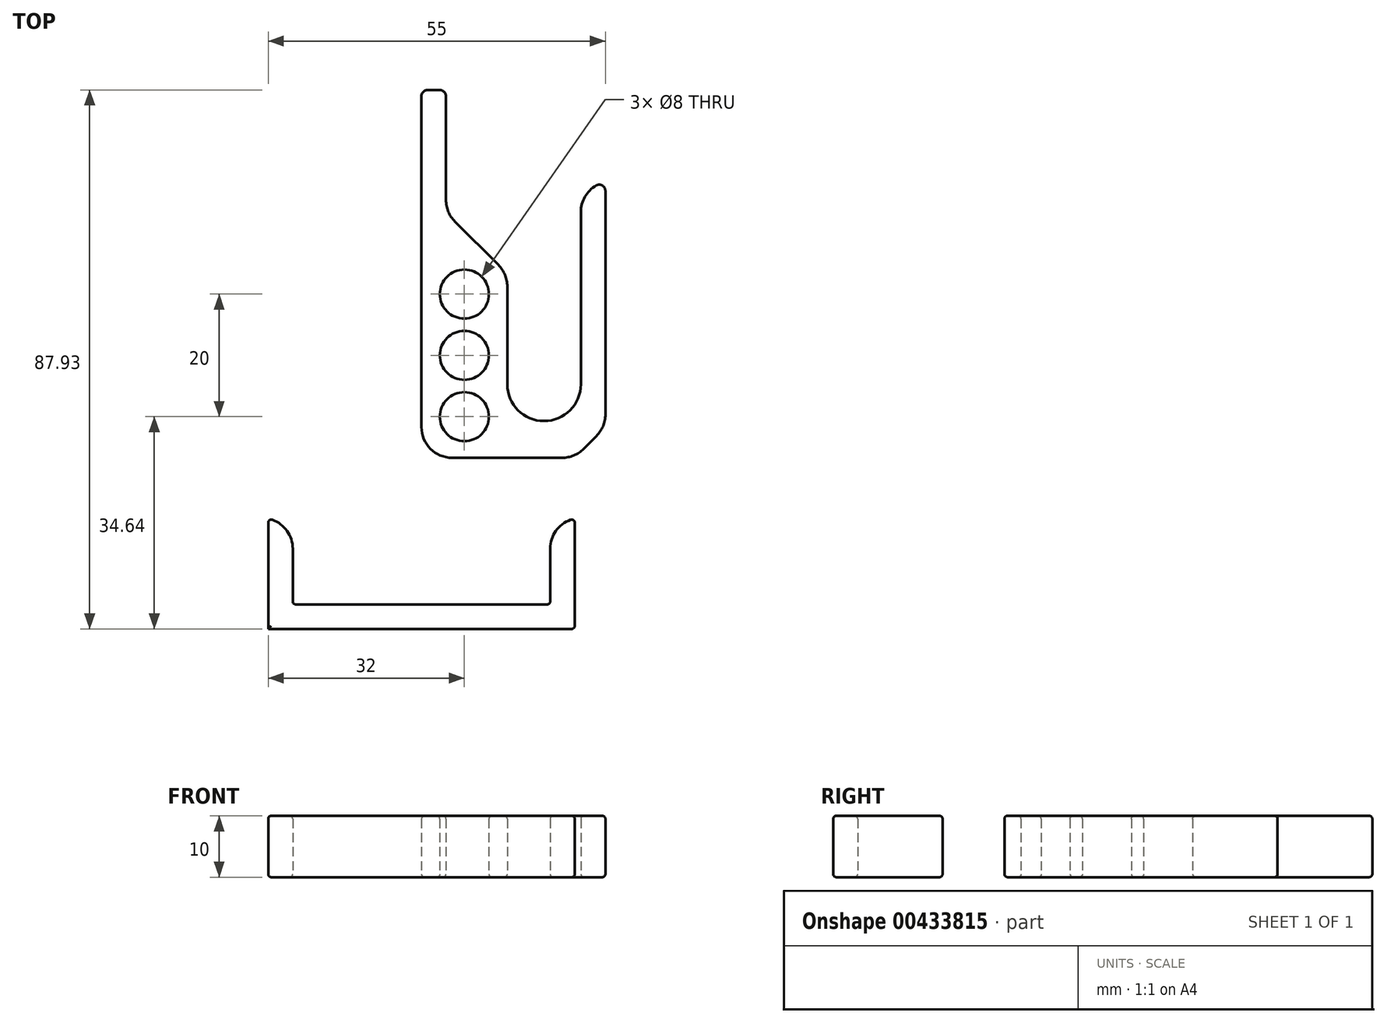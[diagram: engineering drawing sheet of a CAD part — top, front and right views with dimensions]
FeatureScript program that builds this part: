
annotation { "Feature Type Name" : "Feature", "Feature Type Description" : "" }
export const myFeature = defineFeature(function(context is Context, id is Id, definition is map)
    precondition{}
    {
        {
            var Q0;
            Q0=qCreatedBy(makeId("Top.planeOp"),FACE);
            var sketch = newSketch(context, id + "F0", { "sketchPlane" : qUnion([Q0])});
            skLineSegment(sketch, "E0", {"start": v(0, 35.79) * mm, "end": v(0, -24.21) * mm});
            skLineSegment(sketch, "E1", {"start": v(0, -24.21) * mm, "end": v(25, -24.21) * mm});
            skLineSegment(sketch, "E2", {"start": v(25, -24.21) * mm, "end": v(30, -19.21) * mm});
            skLineSegment(sketch, "E3", {"start": v(30, -19.21) * mm, "end": v(30, 20.79) * mm});
            skLineSegment(sketch, "E4", {"start": v(30, 20.79) * mm, "end": v(26, 20.79) * mm});
            skLineSegment(sketch, "E5", {"start": v(26, 20.79) * mm, "end": v(26, -12.21) * mm});
            skLineSegment(sketch, "E6", {"start": v(14, -12.21) * mm, "end": v(14, 5.79) * mm});
            skLineSegment(sketch, "E7", {"start": v(4, 35.79) * mm, "end": v(0, 35.79) * mm});
            skLineSegment(sketch, "E8", {"start": v(14, 5.79) * mm, "end": v(4, 15.79) * mm});
            skLineSegment(sketch, "E9", {"start": v(4, 15.79) * mm, "end": v(4, 35.79) * mm});
            skArc(sketch, "E10", {"start": v(14, -12.21) * mm, "mid": v(20, -18.21) * mm, "end": v(26, -12.21) * mm});
            skSolve(sketch);
        }
        {
            var Q0;
            Q0 = qSketchRegion(id + "F0", true);
            extrude(context, id + "F1", {"entities" : qUnion([Q0]), "depth" : 10 * mm});
        }
        {
            var Q0;
            Q0=makeQuery(id+"F1.opExtrude","SWEPT_EDGE",EDGE,{"disambiguationData":[OSD([sQuery(id+"F0.wireOp",EDGE,"E2"),sQuery(id+"F0.wireOp",EDGE,"E3")])]});
            var Q1;
            Q1=makeQuery(id+"F1.opExtrude","SWEPT_EDGE",EDGE,{"disambiguationData":[OSD([sQuery(id+"F0.wireOp",EDGE,"E1"),sQuery(id+"F0.wireOp",EDGE,"E2")])]});
            var Q2;
            Q2=makeQuery(id+"F1.opExtrude","SWEPT_EDGE",EDGE,{"disambiguationData":[OSD([sQuery(id+"F0.wireOp",EDGE,"E0"),sQuery(id+"F0.wireOp",EDGE,"E1")])]});
            var Q3;
            Q3=makeQuery(id+"F1.opExtrude","SWEPT_EDGE",EDGE,{"disambiguationData":[OSD([sQuery(id+"F0.wireOp",EDGE,"k2jaiBP4-kXWV-sNBi-WAxK-4QkH4Nh1HUbv"),sQuery(id+"F0.wireOp",EDGE,"E6")])]});
            var Q4;
            Q4=makeQuery(id+"F1.opExtrude","SWEPT_EDGE",EDGE,{"disambiguationData":[OSD([sQuery(id+"F0.wireOp",EDGE,"0vQgTybP-b8qj-oL10-YA1z-iEbFXQybWoTR"),sQuery(id+"F0.wireOp",EDGE,"k2jaiBP4-kXWV-sNBi-WAxK-4QkH4Nh1HUbv")])]});
            var Q5;
            Q5=makeQuery(id+"F1.opExtrude","SWEPT_EDGE",EDGE,{"disambiguationData":[OSD([sQuery(id+"F0.wireOp",EDGE,"E5"),sQuery(id+"F0.wireOp",EDGE,"0vQgTybP-b8qj-oL10-YA1z-iEbFXQybWoTR")])]});
            var Q6;
            Q6=makeQuery(id+"F1.opExtrude","SWEPT_EDGE",EDGE,{"disambiguationData":[OSD([sQuery(id+"F0.wireOp",EDGE,"E4"),sQuery(id+"F0.wireOp",EDGE,"E5")])]});
            var Q7;
            Q7=makeQuery(id+"F1.opExtrude","SWEPT_EDGE",EDGE,{"disambiguationData":[OSD([sQuery(id+"F0.wireOp",EDGE,"E6"),sQuery(id+"F0.wireOp",EDGE,"E8")])]});
            var Q8;
            Q8=makeQuery(id+"F1.opExtrude","SWEPT_EDGE",EDGE,{"disambiguationData":[OSD([sQuery(id+"F0.wireOp",EDGE,"E8"),sQuery(id+"F0.wireOp",EDGE,"E9")])]});
            fillet(context, id + "F2", {"entities" : qUnion([Q0, Q1, Q2, Q3, Q4, Q5, Q6, Q7, Q8]), "radius" : 5 * mm, "tangentPropagation" : true, "allowEdgeOverflow" : false});
        }
        {
            var Q0;
            Q0=makeQuery(id+"F2.opFillet","BLEND_EDGE",EDGE,{"blendedFrom":[makeQuery(id+"F1.opExtrude","SWEPT_EDGE",EDGE,{"disambiguationData":[OSD([sQuery(id+"F0.wireOp",EDGE,"E4"),sQuery(id+"F0.wireOp",EDGE,"E5")])]}),makeQuery(id+"F1.opExtrude","SWEPT_FACE",FACE,{"disambiguationData":[OSD([sQuery(id+"F0.wireOp",EDGE,"E3")])]})],"blendedInto":[makeQuery(id+"F1.opExtrude","SWEPT_FACE",FACE,{"disambiguationData":[OSD([sQuery(id+"F0.wireOp",EDGE,"E3")])]})]});
            var Q1;
            Q1=makeQuery(id+"F1.opExtrude","SWEPT_EDGE",EDGE,{"disambiguationData":[OSD([sQuery(id+"F0.wireOp",EDGE,"E0"),sQuery(id+"F0.wireOp",EDGE,"E7")])]});
            var Q2;
            Q2=makeQuery(id+"F1.opExtrude","SWEPT_EDGE",EDGE,{"disambiguationData":[OSD([sQuery(id+"F0.wireOp",EDGE,"E7"),sQuery(id+"F0.wireOp",EDGE,"E9")])]});
            fillet(context, id + "F3", {"entities" : qUnion([Q0, Q1, Q2]), "radius" : 1 * mm, "tangentPropagation" : true, "allowEdgeOverflow" : false});
        }
        {
            var Q0;
            Q0=qCreatedBy(makeId("Top.planeOp"),FACE);
            var sketch = newSketch(context, id + "F4", { "sketchPlane" : qUnion([Q0])});
            skCircle(sketch, "E11", {"center": v(7, 2.5) * mm, "radius": 4 * mm});
            skCircle(sketch, "E12", {"center": v(7, -7.5) * mm, "radius": 4 * mm});
            skCircle(sketch, "E13", {"center": v(7, -17.5) * mm, "radius": 4 * mm});
            skSolve(sketch);
        }
        {
            var Q0;
            Q0 = qSketchRegion(id + "F4", true);
            extrude(context, id + "F5", {"entities" : qUnion([Q0]), "depth" : 25 * mm});
        }
        {
            var Q0;
            Q0=makeQuery(id+"F5.opExtrude","SWEPT_BODY",BODY,{"disambiguationData":[OSD([sQuery(id+"F4.wireOp",EDGE,"E13")])]});
            var Q1;
            Q1=makeQuery(id+"F5.opExtrude","SWEPT_BODY",BODY,{"disambiguationData":[OSD([sQuery(id+"F4.wireOp",EDGE,"E12")])]});
            var Q2;
            Q2=makeQuery(id+"F5.opExtrude","SWEPT_BODY",BODY,{"disambiguationData":[OSD([sQuery(id+"F4.wireOp",EDGE,"E11")])]});
            var Q3;
            Q3=makeQuery(id+"F1.opExtrude","SWEPT_BODY",BODY,{"disambiguationData":[OSD([sQuery(id+"F0.wireOp",EDGE,"E0"),sQuery(id+"F0.wireOp",EDGE,"E1"),sQuery(id+"F0.wireOp",EDGE,"E2"),sQuery(id+"F0.wireOp",EDGE,"E3"),sQuery(id+"F0.wireOp",EDGE,"E4"),sQuery(id+"F0.wireOp",EDGE,"E5"),sQuery(id+"F0.wireOp",EDGE,"0vQgTybP-b8qj-oL10-YA1z-iEbFXQybWoTR"),sQuery(id+"F0.wireOp",EDGE,"k2jaiBP4-kXWV-sNBi-WAxK-4QkH4Nh1HUbv"),sQuery(id+"F0.wireOp",EDGE,"E6"),sQuery(id+"F0.wireOp",EDGE,"E7"),sQuery(id+"F0.wireOp",EDGE,"E8"),sQuery(id+"F0.wireOp",EDGE,"E9")])]});
            booleanBodies(context, id + "F6", {"operationType" : BooleanOperationType.SUBTRACTION, "tools" : qUnion([Q0, Q1, Q2]), "targets" : qUnion([Q3])});
        }
        {
            var Q0;
            Q0=makeQuery(id+"F6.opBoolean","INTERSECT",EDGE,{"derivedFrom":[makeQuery(id+"F1.opExtrude","CAP_FACE",FACE,{"disambiguationData":[OSD([sQuery(id+"F0.wireOp",EDGE,"E0"),sQuery(id+"F0.wireOp",EDGE,"E1"),sQuery(id+"F0.wireOp",EDGE,"E2"),sQuery(id+"F0.wireOp",EDGE,"E3"),sQuery(id+"F0.wireOp",EDGE,"E4"),sQuery(id+"F0.wireOp",EDGE,"E5"),sQuery(id+"F0.wireOp",EDGE,"0vQgTybP-b8qj-oL10-YA1z-iEbFXQybWoTR"),sQuery(id+"F0.wireOp",EDGE,"k2jaiBP4-kXWV-sNBi-WAxK-4QkH4Nh1HUbv"),sQuery(id+"F0.wireOp",EDGE,"E6"),sQuery(id+"F0.wireOp",EDGE,"E7"),sQuery(id+"F0.wireOp",EDGE,"E8"),sQuery(id+"F0.wireOp",EDGE,"E9")])],"isStart":false}),makeQuery(id+"F5.opExtrude","SWEPT_FACE",FACE,{"disambiguationData":[OSD([sQuery(id+"F4.wireOp",EDGE,"E13")])]})]});
            var Q1;
            Q1=makeQuery(id+"F6.opBoolean","INTERSECT",EDGE,{"derivedFrom":[makeQuery(id+"F1.opExtrude","CAP_FACE",FACE,{"disambiguationData":[OSD([sQuery(id+"F0.wireOp",EDGE,"E0"),sQuery(id+"F0.wireOp",EDGE,"E1"),sQuery(id+"F0.wireOp",EDGE,"E2"),sQuery(id+"F0.wireOp",EDGE,"E3"),sQuery(id+"F0.wireOp",EDGE,"E4"),sQuery(id+"F0.wireOp",EDGE,"E5"),sQuery(id+"F0.wireOp",EDGE,"0vQgTybP-b8qj-oL10-YA1z-iEbFXQybWoTR"),sQuery(id+"F0.wireOp",EDGE,"k2jaiBP4-kXWV-sNBi-WAxK-4QkH4Nh1HUbv"),sQuery(id+"F0.wireOp",EDGE,"E6"),sQuery(id+"F0.wireOp",EDGE,"E7"),sQuery(id+"F0.wireOp",EDGE,"E8"),sQuery(id+"F0.wireOp",EDGE,"E9")])],"isStart":false}),makeQuery(id+"F5.opExtrude","SWEPT_FACE",FACE,{"disambiguationData":[OSD([sQuery(id+"F4.wireOp",EDGE,"E12")])]})]});
            var Q2;
            Q2=makeQuery(id+"F6.opBoolean","INTERSECT",EDGE,{"derivedFrom":[makeQuery(id+"F1.opExtrude","CAP_FACE",FACE,{"disambiguationData":[OSD([sQuery(id+"F0.wireOp",EDGE,"E0"),sQuery(id+"F0.wireOp",EDGE,"E1"),sQuery(id+"F0.wireOp",EDGE,"E2"),sQuery(id+"F0.wireOp",EDGE,"E3"),sQuery(id+"F0.wireOp",EDGE,"E4"),sQuery(id+"F0.wireOp",EDGE,"E5"),sQuery(id+"F0.wireOp",EDGE,"0vQgTybP-b8qj-oL10-YA1z-iEbFXQybWoTR"),sQuery(id+"F0.wireOp",EDGE,"k2jaiBP4-kXWV-sNBi-WAxK-4QkH4Nh1HUbv"),sQuery(id+"F0.wireOp",EDGE,"E6"),sQuery(id+"F0.wireOp",EDGE,"E7"),sQuery(id+"F0.wireOp",EDGE,"E8"),sQuery(id+"F0.wireOp",EDGE,"E9")])],"isStart":false}),makeQuery(id+"F5.opExtrude","SWEPT_FACE",FACE,{"disambiguationData":[OSD([sQuery(id+"F4.wireOp",EDGE,"E11")])]})]});
            var Q3;
            Q3=makeQuery(id+"F6.opBoolean","COPY",EDGE,{"derivedFrom":makeQuery(id+"F5.opExtrude","CAP_EDGE",EDGE,{"disambiguationData":[OSD([sQuery(id+"F4.wireOp",EDGE,"E11")])],"isStart":true})});
            var Q4;
            Q4=makeQuery(id+"F6.opBoolean","COPY",EDGE,{"derivedFrom":makeQuery(id+"F5.opExtrude","CAP_EDGE",EDGE,{"disambiguationData":[OSD([sQuery(id+"F4.wireOp",EDGE,"E12")])],"isStart":true})});
            var Q5;
            Q5=makeQuery(id+"F6.opBoolean","COPY",EDGE,{"derivedFrom":makeQuery(id+"F5.opExtrude","CAP_EDGE",EDGE,{"disambiguationData":[OSD([sQuery(id+"F4.wireOp",EDGE,"E13")])],"isStart":true})});
            var Q6;
            Q6=makeQuery(id+"F1.opExtrude","CAP_FACE",FACE,{"disambiguationData":[OSD([sQuery(id+"F0.wireOp",EDGE,"E0"),sQuery(id+"F0.wireOp",EDGE,"E1"),sQuery(id+"F0.wireOp",EDGE,"E2"),sQuery(id+"F0.wireOp",EDGE,"E3"),sQuery(id+"F0.wireOp",EDGE,"E4"),sQuery(id+"F0.wireOp",EDGE,"E5"),sQuery(id+"F0.wireOp",EDGE,"0vQgTybP-b8qj-oL10-YA1z-iEbFXQybWoTR"),sQuery(id+"F0.wireOp",EDGE,"k2jaiBP4-kXWV-sNBi-WAxK-4QkH4Nh1HUbv"),sQuery(id+"F0.wireOp",EDGE,"E6"),sQuery(id+"F0.wireOp",EDGE,"E7"),sQuery(id+"F0.wireOp",EDGE,"E8"),sQuery(id+"F0.wireOp",EDGE,"E9")])],"isStart":true});
            var Q7;
            Q7=makeQuery(id+"F1.opExtrude","CAP_FACE",FACE,{"disambiguationData":[OSD([sQuery(id+"F0.wireOp",EDGE,"E0"),sQuery(id+"F0.wireOp",EDGE,"E1"),sQuery(id+"F0.wireOp",EDGE,"E2"),sQuery(id+"F0.wireOp",EDGE,"E3"),sQuery(id+"F0.wireOp",EDGE,"E4"),sQuery(id+"F0.wireOp",EDGE,"E5"),sQuery(id+"F0.wireOp",EDGE,"0vQgTybP-b8qj-oL10-YA1z-iEbFXQybWoTR"),sQuery(id+"F0.wireOp",EDGE,"k2jaiBP4-kXWV-sNBi-WAxK-4QkH4Nh1HUbv"),sQuery(id+"F0.wireOp",EDGE,"E6"),sQuery(id+"F0.wireOp",EDGE,"E7"),sQuery(id+"F0.wireOp",EDGE,"E8"),sQuery(id+"F0.wireOp",EDGE,"E9")])],"isStart":false});
            fillet(context, id + "F7", {"entities" : qUnion([Q0, Q1, Q2, Q3, Q4, Q5, Q6, Q7]), "radius" : 0.5 * mm, "tangentPropagation" : true, "allowEdgeOverflow" : false});
        }
        {
            var Q0;
            Q0=qCreatedBy(makeId("Top.planeOp"),FACE);
            var sketch = newSketch(context, id + "F8", { "sketchPlane" : qUnion([Q0])});
            skLineSegment(sketch, "E14", {"start": v(-25, -34.14) * mm, "end": v(-25, -52.14) * mm});
            skLineSegment(sketch, "E15", {"start": v(-25, -52.14) * mm, "end": v(25, -52.14) * mm});
            skLineSegment(sketch, "E16", {"start": v(25, -52.14) * mm, "end": v(25, -34.14) * mm});
            skLineSegment(sketch, "E17", {"start": v(25, -34.14) * mm, "end": v(21, -34.14) * mm});
            skLineSegment(sketch, "E18", {"start": v(21, -34.14) * mm, "end": v(21, -48.14) * mm});
            skLineSegment(sketch, "E19", {"start": v(21, -48.14) * mm, "end": v(-21, -48.14) * mm});
            skLineSegment(sketch, "E20", {"start": v(-21, -48.14) * mm, "end": v(-21, -34.14) * mm});
            skLineSegment(sketch, "E21", {"start": v(-21, -34.14) * mm, "end": v(-25, -34.14) * mm});
            skSolve(sketch);
        }
        {
            var Q0;
            Q0 = qSketchRegion(id + "F8", true);
            extrude(context, id + "F9", {"entities" : qUnion([Q0]), "depth" : 10 * mm});
        }
        {
            var Q0;
            Q0=makeQuery(id+"F9.opExtrude","SWEPT_EDGE",EDGE,{"disambiguationData":[OSD([sQuery(id+"F8.wireOp",EDGE,"E17"),sQuery(id+"F8.wireOp",EDGE,"E18")])]});
            var Q1;
            Q1=makeQuery(id+"F9.opExtrude","SWEPT_EDGE",EDGE,{"disambiguationData":[OSD([sQuery(id+"F8.wireOp",EDGE,"E20"),sQuery(id+"F8.wireOp",EDGE,"E21")])]});
            fillet(context, id + "F10", {"entities" : qUnion([Q0, Q1]), "radius" : 5 * mm, "tangentPropagation" : true, "allowEdgeOverflow" : false});
        }
        {
            var Q0;
            Q0=makeQuery(id+"F9.opExtrude","SWEPT_EDGE",EDGE,{"disambiguationData":[OSD([sQuery(id+"F8.wireOp",EDGE,"E15"),sQuery(id+"F8.wireOp",EDGE,"E16")])]});
            var Q1;
            Q1=makeQuery(id+"F10.opFillet","BLEND_EDGE",EDGE,{"blendedFrom":[makeQuery(id+"F9.opExtrude","SWEPT_EDGE",EDGE,{"disambiguationData":[OSD([sQuery(id+"F8.wireOp",EDGE,"E17"),sQuery(id+"F8.wireOp",EDGE,"E18")])]}),makeQuery(id+"F9.opExtrude","SWEPT_FACE",FACE,{"disambiguationData":[OSD([sQuery(id+"F8.wireOp",EDGE,"E16")])]})],"blendedInto":[makeQuery(id+"F9.opExtrude","SWEPT_FACE",FACE,{"disambiguationData":[OSD([sQuery(id+"F8.wireOp",EDGE,"E16")])]})]});
            var Q2;
            Q2=makeQuery(id+"F10.opFillet","BLEND_EDGE",EDGE,{"blendedFrom":[makeQuery(id+"F9.opExtrude","SWEPT_EDGE",EDGE,{"disambiguationData":[OSD([sQuery(id+"F8.wireOp",EDGE,"E20"),sQuery(id+"F8.wireOp",EDGE,"E21")])]}),makeQuery(id+"F9.opExtrude","SWEPT_FACE",FACE,{"disambiguationData":[OSD([sQuery(id+"F8.wireOp",EDGE,"E14")])]})],"blendedInto":[makeQuery(id+"F9.opExtrude","SWEPT_FACE",FACE,{"disambiguationData":[OSD([sQuery(id+"F8.wireOp",EDGE,"E14")])]})]});
            var Q3;
            Q3=makeQuery(id+"F9.opExtrude","CAP_EDGE",EDGE,{"disambiguationData":[OSD([sQuery(id+"F8.wireOp",EDGE,"E19")])],"isStart":false});
            var Q4;
            Q4=makeQuery(id+"F9.opExtrude","CAP_EDGE",EDGE,{"disambiguationData":[OSD([sQuery(id+"F8.wireOp",EDGE,"E19")])],"isStart":true});
            var Q5;
            Q5=makeQuery(id+"F9.opExtrude","CAP_FACE",FACE,{"disambiguationData":[OSD([sQuery(id+"F8.wireOp",EDGE,"E14"),sQuery(id+"F8.wireOp",EDGE,"E15"),sQuery(id+"F8.wireOp",EDGE,"E16"),sQuery(id+"F8.wireOp",EDGE,"E17"),sQuery(id+"F8.wireOp",EDGE,"E18"),sQuery(id+"F8.wireOp",EDGE,"E19"),sQuery(id+"F8.wireOp",EDGE,"E20"),sQuery(id+"F8.wireOp",EDGE,"E21")])],"isStart":false});
            var Q6;
            Q6=makeQuery(id+"F9.opExtrude","CAP_FACE",FACE,{"disambiguationData":[OSD([sQuery(id+"F8.wireOp",EDGE,"E14"),sQuery(id+"F8.wireOp",EDGE,"E15"),sQuery(id+"F8.wireOp",EDGE,"E16"),sQuery(id+"F8.wireOp",EDGE,"E17"),sQuery(id+"F8.wireOp",EDGE,"E18"),sQuery(id+"F8.wireOp",EDGE,"E19"),sQuery(id+"F8.wireOp",EDGE,"E20"),sQuery(id+"F8.wireOp",EDGE,"E21")])],"isStart":true});
            var Q7;
            Q7=makeQuery(id+"F9.opExtrude","SWEPT_EDGE",EDGE,{"disambiguationData":[OSD([sQuery(id+"F8.wireOp",EDGE,"E19"),sQuery(id+"F8.wireOp",EDGE,"E20")])]});
            var Q8;
            Q8=makeQuery(id+"F9.opExtrude","SWEPT_EDGE",EDGE,{"disambiguationData":[OSD([sQuery(id+"F8.wireOp",EDGE,"E18"),sQuery(id+"F8.wireOp",EDGE,"E19")])]});
            fillet(context, id + "F11", {"entities" : qUnion([Q0, Q1, Q2, Q3, Q4, Q5, Q6, Q7, Q8]), "radius" : .5 * mm, "tangentPropagation" : true, "allowEdgeOverflow" : false});
        }
    });
